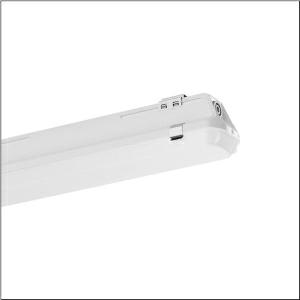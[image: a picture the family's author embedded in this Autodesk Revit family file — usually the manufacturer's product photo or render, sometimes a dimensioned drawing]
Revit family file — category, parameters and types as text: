
# Revit family: monsun_r__21_51fb10dp480b_f32f
name_source: partatom
category: Lighting Fixtures
units: mm (PartAtom-declared; Revit-internal decimal feet)

## family parameters
Cut with Voids When Loaded = No
Host = Face
Light Source = No
Part Type = Normal
Room Calculation Point = No
Round Connector Dimension = Use Diameter
Shared = No

## types (1)
- --- (1 x LED, 8090 lm, 54.4 W, 4000K)
    Apparent Load = 54 VA
    CIE Flux Codes = 47 77 93 94 100
    Color Rendering = 80
    Color Temperature = 4000K
    Default Elevation = 1800 mm
    Description = Monsun® 21, damp-proof luminaire, chain hanger, primary optical cover: enclosure, of PMMA, light emission: direct distribution, primary light characteristic: symmetric, installation type: suspended mounting, surface-mounted, horizontal mounting, vertical mounting, LED, rated luminous flux: 8.090lm, luminous efficacy: 149lm/W, light colour: 840, colour temperature: 4000K, control gear: ECG DALI, with terminal, 5-pole, max. 2.5mm², mains connection: 220..240V, AC, 50/60Hz, rated input power: 54W, housing, of glass-fibre reinforced polyester, uncoated, bright grey, incl. chain hanger, length: 1.590mm, width: 90mm, height: 88mm, clip for enclosure, of stainless steel (V2A), ceiling mounting element, of stainless steel (V2A), chain hanger, of stainless steel (V2A), protection rating (complete): IP66, insulation class (complete): insulation class I (protective earthing), certification: CE, ENEC, VDE, UKCA, protection symbol: D, impact resistance: IK04, permissible operating ambient temperature: -25..+35°C, standard: EN 50419, EN 60598-2-1, corresponds to IFS (International Featured Standards) requirements for safety and quality in the food industry, for indoor or canopied outdoor use, no direct snow, no direct sun, no direct rain, contact your sales advisor before using the luminaires in applications with unclear chemical exposure, large temperature fluctuations or condensation-forming humidity, LABS conformity tested according to VDMA 24364:2018-05, packaging unit: 1 piece
    Height = 89 mm
    Lamp = 1 x LED
    Lamp Light Flux = 8090 lm
    Lamp Power = 54.4 W
    Lamp count = 1
    Length = 1590 mm
    Luminous efficacy = 149 lm/W
    Manufacturer = Siteco
    ModVariant = No
    Model = 51FB10DP480B
    Mounting Place = Ceiling
    Mounting Type = Surface mounted
    Number of Poles = 1
    OnlyDefault = Yes
    Power Factor = 1
    Product Name = Monsun® 21
    Product group = damp-proof luminaire
    ProductGroupID = 300
    Protection Class = Protection class I
    Protection Degree = IP 66
    RLX_Detail_Level = 1
    RLX_Emergency_Light_Flux = 0 lm
    RLX_Emergency_Type = 0
    RLX_Emergency_Type_DB = No
    RlxData = <blob elided: 92421 chars, md5=e9a31b5f>
    Socket = socket
    Standby Power = 0 W
    System Light Flux = 8090 lm
    System Power = 54 W
    Type Comments = factory setting: luminous flux: 100 % | dim-lin: 254 | 358 mA
    Type Image = l_1006717.jpg
    URL = http://relux.com
    VarID = @adj_134465
    Voltage = 0 V
    Weight = 0.00 kg
    Width = 90 mm

## geometry (parser evidence)
native form markers: Blend x4, Sweep x15
no freeform markers — native parametric forms only
